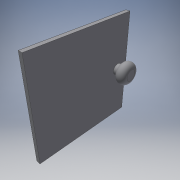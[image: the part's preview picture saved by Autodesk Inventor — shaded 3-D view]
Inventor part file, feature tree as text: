
AUTODESK INVENTOR PART (.ipt)
format: ipt  version: 2016 (Build 200138000, 138)  size: 114,176 bytes
history: native  units: in
note: dims shown in document units (in); Inventor stores cm internally (conversion verified against a paired STEP export)
features: extrude x3, sketch x3, fillet x1
ambient origin geometry x8: Origin, YZ Plane, XZ Plane, XY Plane, X Axis, Y Axis, Z Axis, Center Point
bodies: Solid1 (feature_tree)
feature tree (7):
  extrude  "Extrusion1"  Depth=18.5in
  extrude  "Extrusion2"  Depth=0.75in
  extrude  "Extrusion3"  Depth=0.75in TaperAngle=0.0deg
  fillet  "Fillet1"  Radius=2.0in
  sketch  "Sketch1"  dims[d0=18.0in d1=18.5in]
  sketch  "Sketch2"  dims[d2=0.75in d3=0.0in d4=2.0in]
  sketch  "Sketch3"  dims[d5=2.0in d6=0.75in d7=0.0in d8=2.0in d9=4.0in d10=2.0in d11=0.0in d12=1.0in]
